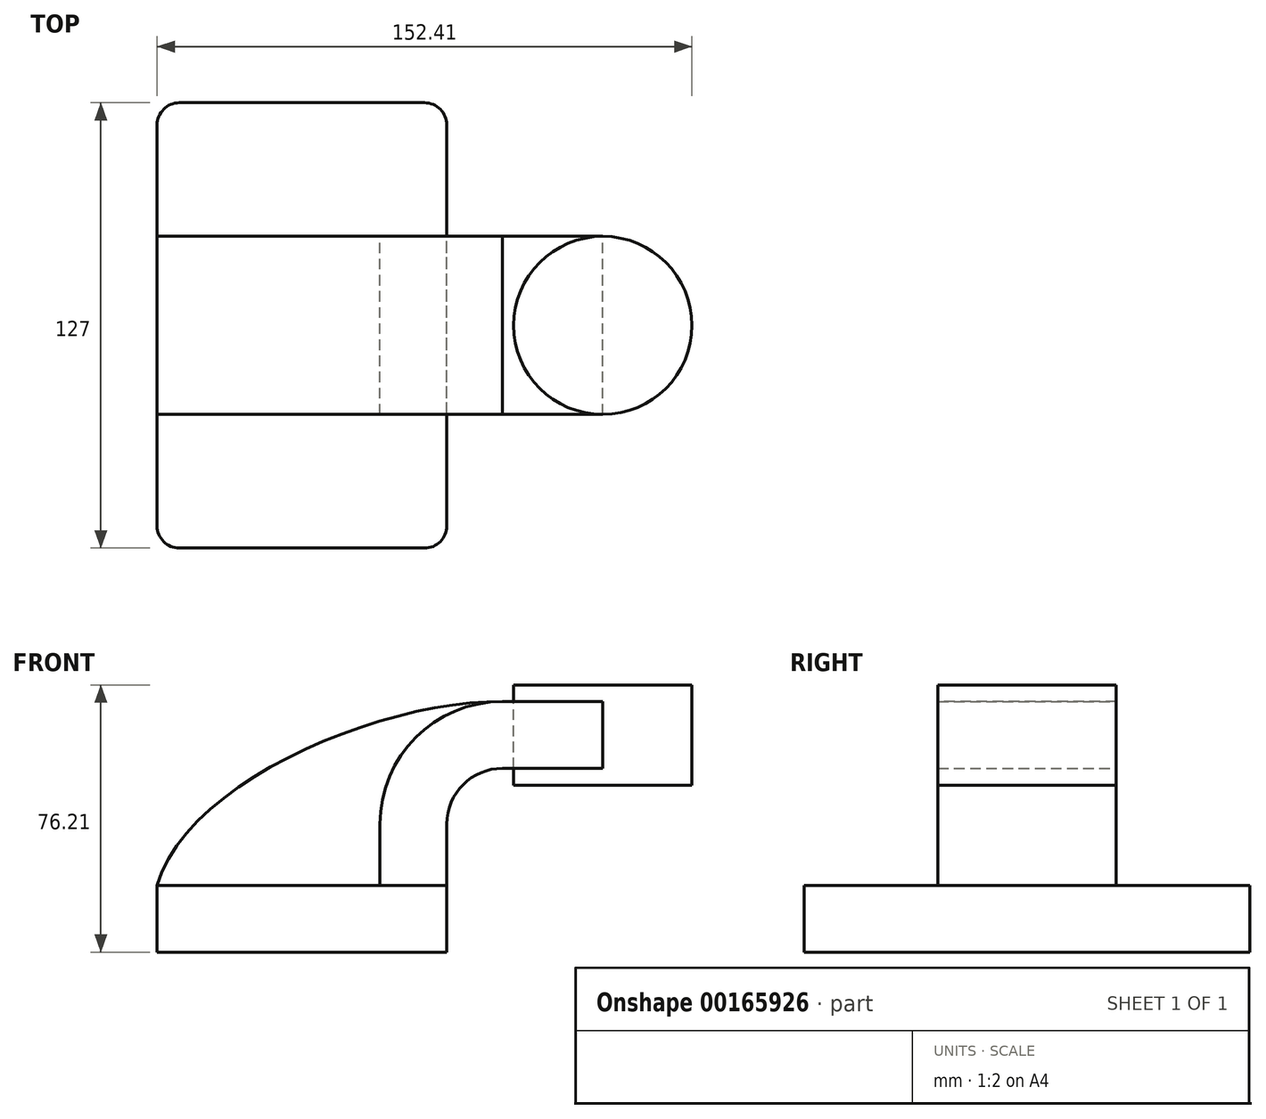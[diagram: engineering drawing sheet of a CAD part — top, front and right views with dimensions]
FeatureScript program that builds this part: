
annotation { "Feature Type Name" : "Feature", "Feature Type Description" : "" }
export const myFeature = defineFeature(function(context is Context, id is Id, definition is map)
    precondition{}
    {
        {
            var Q0;
            Q0=qCreatedBy(makeId("Front.planeOp"),FACE);
            var sketch = newSketch(context, id + "F0", { "sketchPlane" : qUnion([Q0])});
            skLineSegment(sketch, "E0.bottom", {"start": v(-41.27, -9.52) * mm, "end": v(41.28, -9.53) * mm});
            skLineSegment(sketch, "E0.top", {"start": v(-41.27, 9.53) * mm, "end": v(41.28, 9.53) * mm});
            skLineSegment(sketch, "E0.left", {"start": v(-41.27, -9.52) * mm, "end": v(-41.27, 9.53) * mm});
            skLineSegment(sketch, "E0.right", {"start": v(41.28, -9.53) * mm, "end": v(41.27, 9.53) * mm});
            skPoint(sketch, "E0.middle", {"position": v(0, 0) * mm});
            skLineSegment(sketch, "E1.bottom", {"start": v(111.12, 38.1) * mm, "end": v(60.33, 38.1) * mm});
            skLineSegment(sketch, "E1.top", {"start": v(111.13, 66.67) * mm, "end": v(60.33, 66.67) * mm});
            skLineSegment(sketch, "E1.left", {"start": v(111.13, 38.1) * mm, "end": v(111.13, 66.67) * mm});
            skPoint(sketch, "E1.middle", {"position": v(85.73, 52.39) * mm});
            skLineSegment(sketch, "E2", {"start": v(41.27, 9.53) * mm, "end": v(41.27, 27) * mm});
            skArc(sketch, "E3", {"start": v(41.27, 27) * mm, "mid": v(45.92, 38.23) * mm, "end": v(57.15, 42.88) * mm});
            skLineSegment(sketch, "E4", {"start": v(57.15, 42.88) * mm, "end": v(85.73, 42.88) * mm});
            skLineSegment(sketch, "E5.0", {"start": v(57.15, 61.93) * mm, "end": v(85.73, 61.93) * mm});
            skArc(sketch, "E5.1", {"start": v(22.23, 27) * mm, "mid": v(32.45, 51.7) * mm, "end": v(57.15, 61.93) * mm});
            skLineSegment(sketch, "E5.2", {"start": v(22.23, 9.53) * mm, "end": v(22.23, 27) * mm});
            skLineSegment(sketch, "E6", {"start": v(85.73, 61.93) * mm, "end": v(85.73, 42.88) * mm});
            skFitSpline(sketch, "E7", {"points": [v(-41.28, 9.53) * mm, v(57.15, 61.93) * mm], "startDerivative": vector(25, 89.47) * mm, "endDerivative": vector(101.27, -1.4) * mm});
            skLineSegment(sketch, "E8.0", {"start": v(57.15, 61.93) * mm, "end": v(67.41, 61.93) * mm});
            skLineSegment(sketch, "E8.2", {"start": v(22.22, 9.53) * mm, "end": v(22.22, 27) * mm});
            skLineSegment(sketch, "E9", {"start": v(60.32, 66.67) * mm, "end": v(60.33, 38.1) * mm});
            skLineSegment(sketch, "E10", {"start": v(85.72, 66.67) * mm, "end": v(85.72, 38.1) * mm});
            skSolve(sketch);
        }
        {
            var Q0;
            Q0=makeQuery(id+"F0.imprint","IMPRINT",FACE,{"disambiguationData":[TD([[makeQuery(id+"F0.imprint","IMPRINT",EDGE,{"derivedFrom":sQuery(id+"F0.wireOp",EDGE,"E0.bottom")}),1.0]])]});
            var Q1;
            Q1 = qSketchRegion(id + "FxqkvIaHf40T7x3_0", true);
            extrude(context, id + "F1", {"entities" : qUnion([Q0, Q1]), "endBound" : BoundingType.SYMMETRIC, "depth" : 127 * mm});
        }
        {
            var Q0;
            {var subQ1=sQuery(id+"F0.wireOp",EDGE,"E2");Q0=makeQuery(id+"F0.imprint","IMPRINT",FACE,{"disambiguationData":[TD([[makeQuery(id+"F0.imprint","IMPRINT",EDGE,{"derivedFrom":subQ1}),1.0]])]});}
            var Q1;
            {var subQ5=sQuery(id+"F0.wireOp",EDGE,"E6");Q1=makeQuery(id+"F0.imprint","IMPRINT",FACE,{"disambiguationData":[TD([[makeQuery(id+"F0.imprint","IMPRINT",EDGE,{"derivedFrom":subQ5}),-1.0]])]});}
            var Q2;
            {var subQ5=sQuery(id+"F0.wireOp",EDGE,"E5.0");Q2=makeQuery(id+"F0.imprint","IMPRINT",FACE,{"disambiguationData":[TD([[makeQuery(id+"F0.imprint","IMPRINT",EDGE,{"derivedFrom":subQ5}),-1.0]])]});}
            extrude(context, id + "F2", {"entities" : qUnion([Q0, Q1, Q2]), "endBound" : BoundingType.SYMMETRIC, "depth" : 50.8 * mm});
        }
        {
            var Q0;
            {var subQ0=sQuery(id+"F0.wireOp",EDGE,"E7");Q0=makeQuery(id+"F0.imprint","IMPRINT",FACE,{"disambiguationData":[TD([[makeQuery(id+"F0.imprint","IMPRINT",EDGE,{"derivedFrom":subQ0}),-1.0]])]});}
            extrude(context, id + "F3", {"entities" : qUnion([Q0]), "endBound" : BoundingType.SYMMETRIC, "depth" : 50.8 * mm});
        }
        {
            var Q0;
            {var subQ4=sQuery(id+"F0.wireOp",EDGE,"E1.left");Q0=makeQuery(id+"F0.imprint","IMPRINT",FACE,{"disambiguationData":[TD([[makeQuery(id+"F0.imprint","IMPRINT",EDGE,{"derivedFrom":subQ4}),1.0]])]});}
            var Q1;
            Q1=sQuery(id+"F0.wireOp",EDGE,"E6");
            revolve(context, id + "F4", {"entities" : qUnion([Q0]), "axis" : qUnion([Q1]), "revolveType" : RevolveType.FULL});
        }
        {
            var Q0;
            Q0=makeQuery(id+"F1.opExtrude","CAP_EDGE",EDGE,{"disambiguationData":[OSD([sQuery(id+"F0.wireOp",EDGE,"E0.left")])],"isStart":false});
            var Q1;
            Q1=makeQuery(id+"F1.opExtrude","CAP_EDGE",EDGE,{"disambiguationData":[OSD([sQuery(id+"F0.wireOp",EDGE,"E0.right")])],"isStart":false});
            var Q2;
            Q2=makeQuery(id+"F1.opExtrude","CAP_EDGE",EDGE,{"disambiguationData":[OSD([sQuery(id+"F0.wireOp",EDGE,"E0.right")])],"isStart":true});
            var Q3;
            Q3=makeQuery(id+"F1.opExtrude","CAP_EDGE",EDGE,{"disambiguationData":[OSD([sQuery(id+"F0.wireOp",EDGE,"E0.left")])],"isStart":true});
            fillet(context, id + "F5", {"entities" : qUnion([Q0, Q1, Q2, Q3]), "radius" : 6.35 * mm, "tangentPropagation" : true, "allowEdgeOverflow" : false});
        }
    });
